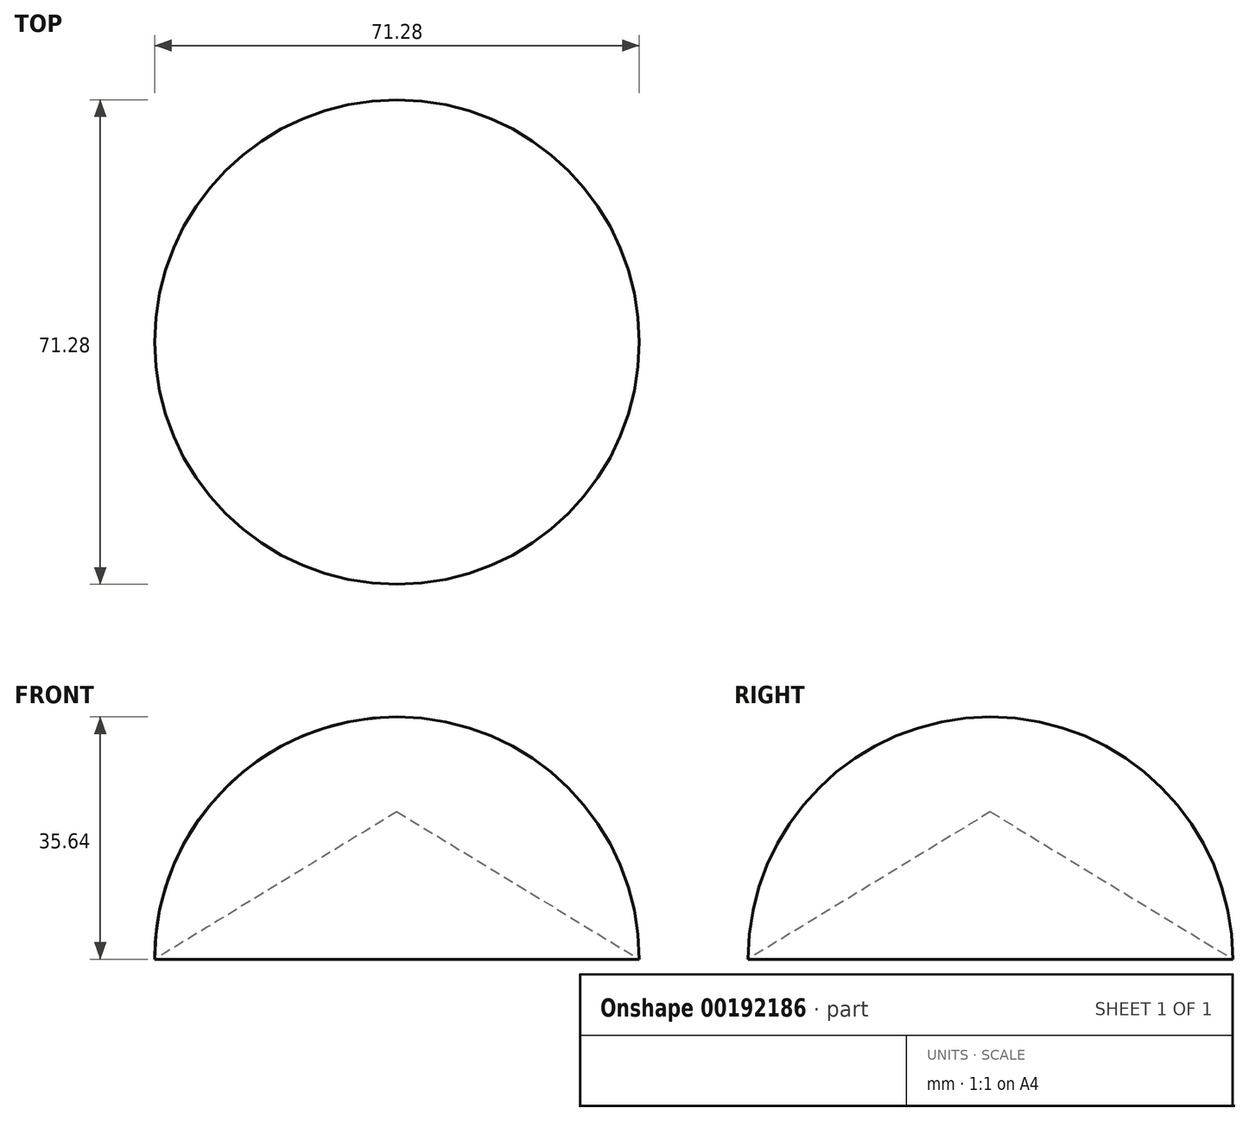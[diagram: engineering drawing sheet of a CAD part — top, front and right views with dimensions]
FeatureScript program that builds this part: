
annotation { "Feature Type Name" : "Feature", "Feature Type Description" : "" }
export const myFeature = defineFeature(function(context is Context, id is Id, definition is map)
    precondition{}
    {
        {
            var Q0;
            Q0=qCreatedBy(makeId("Front.planeOp"),FACE);
            var sketch = newSketch(context, id + "F0", { "sketchPlane" : qUnion([Q0])});
            skArc(sketch, "E0", {"start": v(0, 35.64) * mm, "mid": v(-25.2, 25.2) * mm, "end": v(-35.64, 0) * mm});
            skLineSegment(sketch, "E1", {"start": v(-35.64, 0) * mm, "end": v(0, 21.7) * mm});
            skLineSegment(sketch, "E2", {"start": v(0, 21.7) * mm, "end": v(0, 35.64) * mm});
            skPoint(sketch, "E3.orphan", {"position": v(35.64, 0) * mm});
            skSolve(sketch);
        }
        {
            var Q0;
            Q0=makeQuery(id+"F0.imprint","IMPRINT",FACE,{"disambiguationData":[TD([[makeQuery(id+"F0.imprint","IMPRINT",EDGE,{"derivedFrom":sQuery(id+"F0.wireOp",EDGE,"E0")}),1.0]])]});
            var Q1;
            Q1=sQuery(id+"F0.wireOp",EDGE,"E2");
            revolve(context, id + "F1", {"entities" : qUnion([Q0]), "axis" : qUnion([Q1]), "revolveType" : RevolveType.FULL});
        }
    });
